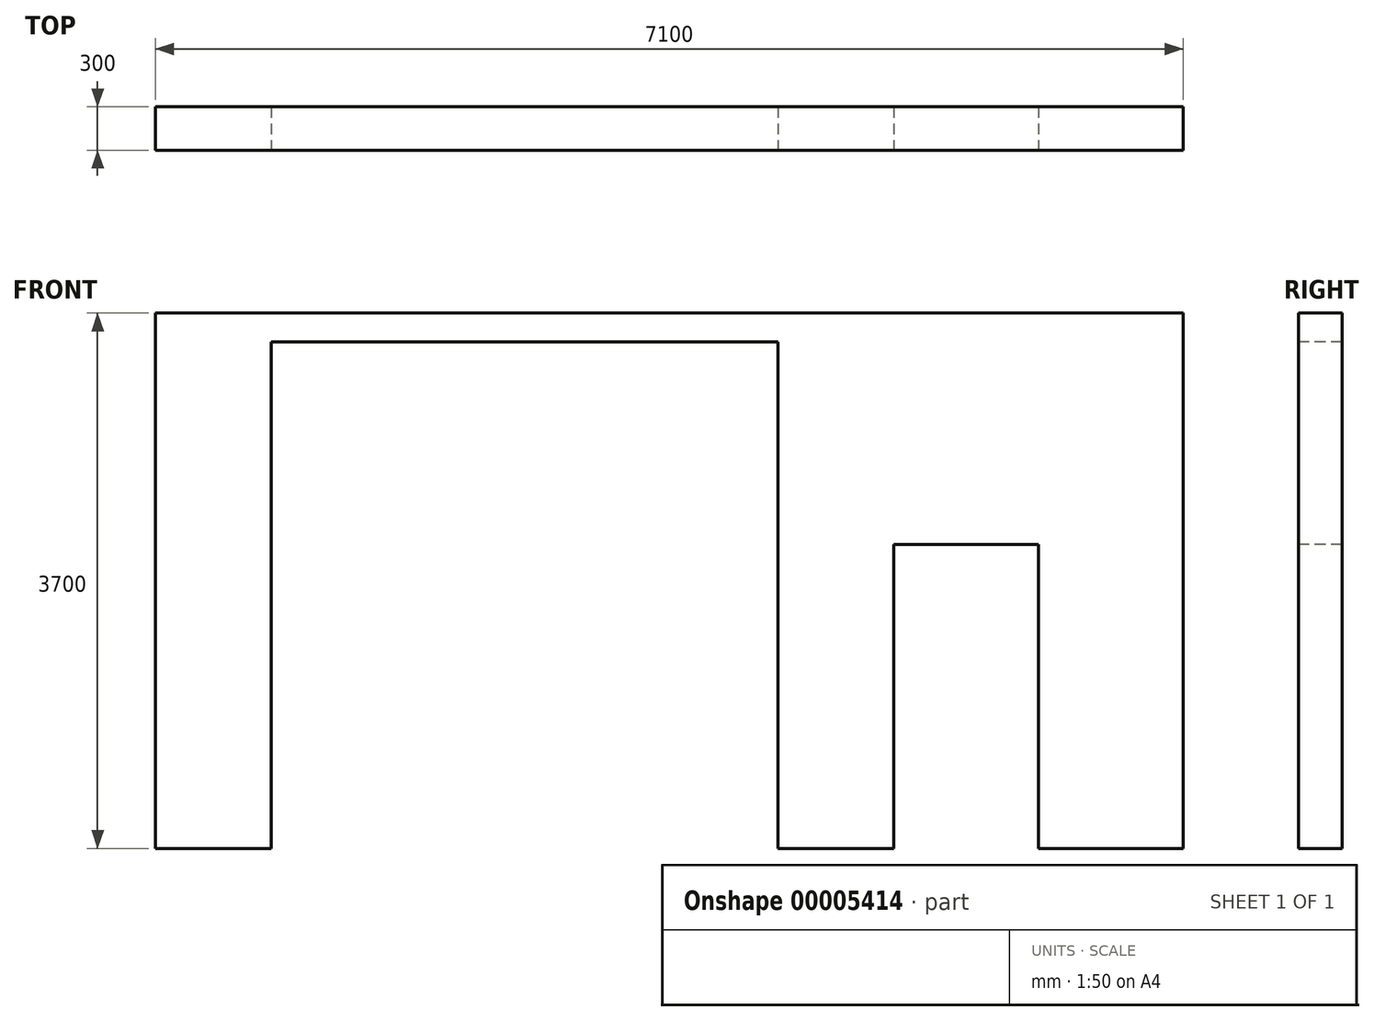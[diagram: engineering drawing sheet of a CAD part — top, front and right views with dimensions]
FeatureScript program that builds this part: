
annotation { "Feature Type Name" : "Feature", "Feature Type Description" : "" }
export const myFeature = defineFeature(function(context is Context, id is Id, definition is map)
    precondition{}
    {
        {
            var Q0;
            Q0=qCreatedBy(makeId("Front.planeOp"),FACE);
            var sketch = newSketch(context, id + "F0", { "sketchPlane" : qUnion([Q0])});
            skLineSegment(sketch, "E0.bottom", {"start": v(-3351.92, 1919.24) * mm, "end": v(3748.08, 1919.24) * mm});
            skLineSegment(sketch, "E0.top", {"start": v(-3351.92, -1780.76) * mm, "end": v(3748.08, -1780.76) * mm});
            skLineSegment(sketch, "E0.left", {"start": v(-3351.92, 1919.24) * mm, "end": v(-3351.92, -1780.76) * mm});
            skLineSegment(sketch, "E0.right", {"start": v(3748.08, 1919.24) * mm, "end": v(3748.08, -1780.76) * mm});
            skSolve(sketch);
        }
        {
            var Q0;
            Q0 = qSketchRegion(id + "F0", true);
            extrude(context, id + "F1", {"entities" : qUnion([Q0]), "depth" : 300 * mm});
        }
        {
            var Q0;
            Q0=makeQuery(id+"F1.opExtrude","CAP_FACE",FACE,{"disambiguationData":[OSD([sQuery(id+"F0.wireOp",EDGE,"E0.bottom"),sQuery(id+"F0.wireOp",EDGE,"E0.top"),sQuery(id+"F0.wireOp",EDGE,"E0.left"),sQuery(id+"F0.wireOp",EDGE,"E0.right")])],"isStart":false});
            var sketch = newSketch(context, id + "F2", { "sketchPlane" : qUnion([Q0])});
            skLineSegment(sketch, "E1.bottom", {"start": v(-2551.92, -1780.76) * mm, "end": v(948.08, -1780.76) * mm});
            skLineSegment(sketch, "E1.top", {"start": v(-2551.92, 1719.24) * mm, "end": v(948.08, 1719.24) * mm});
            skLineSegment(sketch, "E1.left", {"start": v(-2551.92, -1780.76) * mm, "end": v(-2551.92, 1719.24) * mm});
            skLineSegment(sketch, "E1.right", {"start": v(948.08, -1780.76) * mm, "end": v(948.08, 1719.24) * mm});
            skLineSegment(sketch, "E2.bottom", {"start": v(2748.08, -1780.76) * mm, "end": v(1748.08, -1780.76) * mm});
            skLineSegment(sketch, "E2.top", {"start": v(2748.08, 319.24) * mm, "end": v(1748.08, 319.24) * mm});
            skLineSegment(sketch, "E2.left", {"start": v(2748.08, -1780.76) * mm, "end": v(2748.08, 319.24) * mm});
            skLineSegment(sketch, "E2.right", {"start": v(1748.08, -1780.76) * mm, "end": v(1748.08, 319.24) * mm});
            skSolve(sketch);
        }
        {
            var Q0;
            Q0=makeQuery(id+"F2.imprint","IMPRINT",FACE,{"disambiguationData":[TD([[makeQuery(id+"F2.imprint","IMPRINT",EDGE,{"derivedFrom":sQuery(id+"F2.wireOp",EDGE,"E1.bottom")}),1.0]])]});
            var Q1;
            Q1=makeQuery(id+"F2.imprint","IMPRINT",FACE,{"disambiguationData":[TD([[makeQuery(id+"F2.imprint","IMPRINT",EDGE,{"derivedFrom":sQuery(id+"F2.wireOp",EDGE,"E2.bottom")}),1.0]])]});
            extrude(context, id + "F3", {"entities" : qUnion([Q0, Q1]), "operationType" : NewBodyOperationType.REMOVE, "endBound" : BoundingType.THROUGH_ALL, "oppositeDirection" : true, "depth" : 25 * mm});
        }
    });
